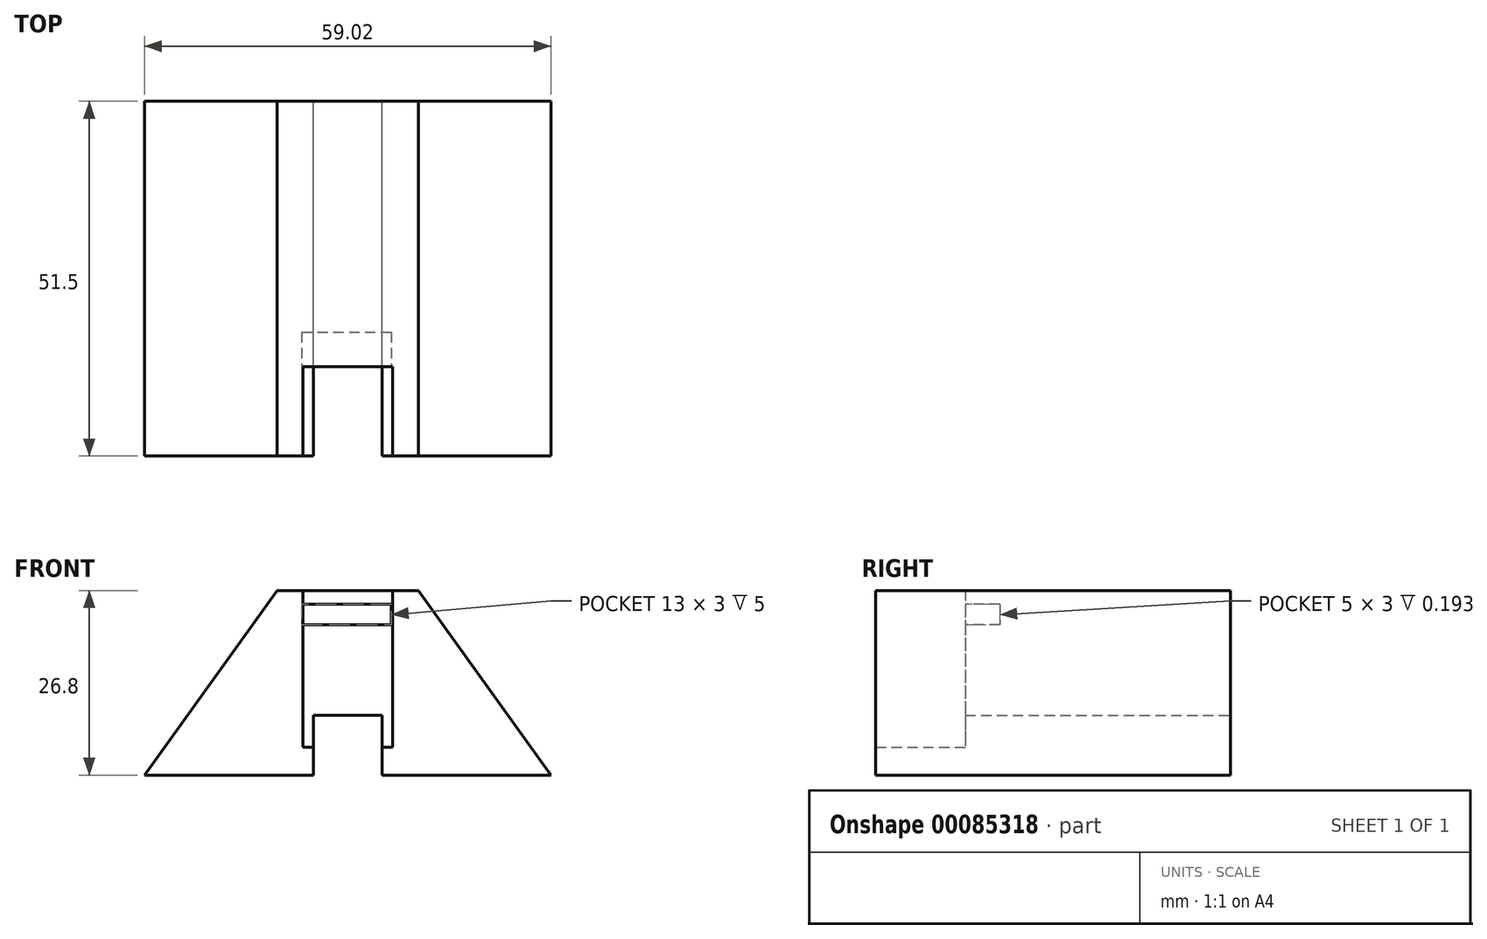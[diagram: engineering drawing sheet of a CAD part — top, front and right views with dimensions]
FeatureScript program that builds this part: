
annotation { "Feature Type Name" : "Feature", "Feature Type Description" : "" }
export const myFeature = defineFeature(function(context is Context, id is Id, definition is map)
    precondition{}
    {
        {
            var Q0;
            Q0=qCreatedBy(makeId("Front.planeOp"),FACE);
            var sketch = newSketch(context, id + "F0", { "sketchPlane" : qUnion([Q0])});
            skLineSegment(sketch, "E0", {"start": v(29.5, 0) * mm, "end": v(10.25, 26.8) * mm});
            skLineSegment(sketch, "E1", {"start": v(10.25, 26.8) * mm, "end": v(-10.25, 26.8) * mm});
            skLineSegment(sketch, "E2", {"start": v(-10.25, 26.8) * mm, "end": v(-29.5, 0) * mm});
            skLineSegment(sketch, "E3.bottom", {"start": v(-5, 8.67) * mm, "end": v(5, 8.67) * mm});
            skLineSegment(sketch, "E3.left", {"start": v(-5, 8.67) * mm, "end": v(-5, 0) * mm});
            skLineSegment(sketch, "E3.right", {"start": v(5, 8.67) * mm, "end": v(5, 0) * mm});
            skLineSegment(sketch, "E4.trimOffspring", {"start": v(5, 0) * mm, "end": v(29.5, 0) * mm});
            skLineSegment(sketch, "E5", {"start": v(-29.5, 0) * mm, "end": v(-5, 0) * mm});
            skSolve(sketch);
        }
        {
            var Q0;
            Q0 = qSketchRegion(id + "F0", true);
            extrude(context, id + "F1", {"entities" : qUnion([Q0]), "depth" : 51.5 * mm});
        }
        {
            var Q0;
            Q0=makeQuery(id+"F1.opExtrude","CAP_FACE",FACE,{"disambiguationData":[OSD([sQuery(id+"F0.wireOp",EDGE,"E0"),sQuery(id+"F0.wireOp",EDGE,"E1"),sQuery(id+"F0.wireOp",EDGE,"E2"),sQuery(id+"F0.wireOp",EDGE,"E3.bottom"),sQuery(id+"F0.wireOp",EDGE,"E3.left"),sQuery(id+"F0.wireOp",EDGE,"E3.right"),sQuery(id+"F0.wireOp",EDGE,"E4.trimOffspring"),sQuery(id+"F0.wireOp",EDGE,"E5")])],"isStart":false});
            var sketch = newSketch(context, id + "F2", { "sketchPlane" : qUnion([Q0])});
            skLineSegment(sketch, "E6.bottom", {"start": v(-6.5, 26.8) * mm, "end": v(6.5, 26.8) * mm});
            skLineSegment(sketch, "E6.top", {"start": v(-6.5, 4.05) * mm, "end": v(6.5, 4.05) * mm});
            skLineSegment(sketch, "E6.left", {"start": v(-6.5, 26.8) * mm, "end": v(-6.5, 4.05) * mm});
            skLineSegment(sketch, "E6.right", {"start": v(6.5, 26.8) * mm, "end": v(6.5, 4.05) * mm});
            skSolve(sketch);
        }
        {
            var Q0;
            Q0 = qSketchRegion(id + "F2", true);
            extrude(context, id + "F3", {"entities" : qUnion([Q0]), "operationType" : NewBodyOperationType.REMOVE, "oppositeDirection" : true, "depth" : 13 * mm});
        }
        {
            var Q0;
            Q0=makeQuery(id+"F3.boolean.opBoolean","COPY",FACE,{"derivedFrom":makeQuery(id+"F3.opExtrude","CAP_FACE",FACE,{"disambiguationData":[OSD([sQuery(id+"F2.wireOp",EDGE,"E6.bottom"),sQuery(id+"F2.wireOp",EDGE,"E6.top"),sQuery(id+"F2.wireOp",EDGE,"E6.left"),sQuery(id+"F2.wireOp",EDGE,"E6.right")])],"isStart":false})});
            var sketch = newSketch(context, id + "F4", { "sketchPlane" : qUnion([Q0])});
            skLineSegment(sketch, "E7.bottom", {"start": v(-6.7, 24.8) * mm, "end": v(6.3, 24.8) * mm});
            skLineSegment(sketch, "E7.top", {"start": v(-6.7, 21.8) * mm, "end": v(6.3, 21.8) * mm});
            skLineSegment(sketch, "E7.left", {"start": v(-6.7, 24.8) * mm, "end": v(-6.7, 21.8) * mm});
            skLineSegment(sketch, "E7.right", {"start": v(6.3, 24.8) * mm, "end": v(6.3, 21.8) * mm});
            skSolve(sketch);
        }
        {
            var Q0;
            Q0 = qSketchRegion(id + "F4", true);
            extrude(context, id + "F5", {"entities" : qUnion([Q0]), "operationType" : NewBodyOperationType.REMOVE, "oppositeDirection" : true, "depth" : 5 * mm});
        }
    });
